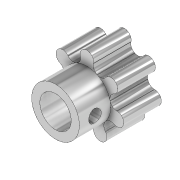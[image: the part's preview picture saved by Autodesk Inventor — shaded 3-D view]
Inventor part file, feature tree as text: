
AUTODESK INVENTOR PART (.ipt)
format: ipt  version: 2020 (Build 240168000, 168)  size: 212,480 bytes
history: native  units: in
note: dims shown in document units (in); Inventor stores cm internally (conversion verified against a paired STEP export)
features: extrude x3, sketch x3
ambient origin geometry x8: Origin, YZ Plane, XZ Plane, XY Plane, X Axis, Y Axis, Z Axis, Center Point
bodies: Solid1 (feature_tree)
feature tree (6):
  extrude  "Extrusion1"  Depth=0.1969in
  extrude  "Extrusion2"  Depth=0.084in
  extrude  "Extrusion3"  Depth=0.1969in
  sketch  "Sketch1"  dims[d0=0.1969in d1=0.4724in]
  sketch  "Sketch2"  dims[d2=0.0866in d5=0.084in]
  sketch  "Sketch3"  dims[d6=0.084in d7=0.084in d8=2.7559in d10=360.0deg d12=0.2362in d13=0.0in d14=0.1969in d15=0.0in d16=0.0787in d17=0.1575in d18=0.0in]
